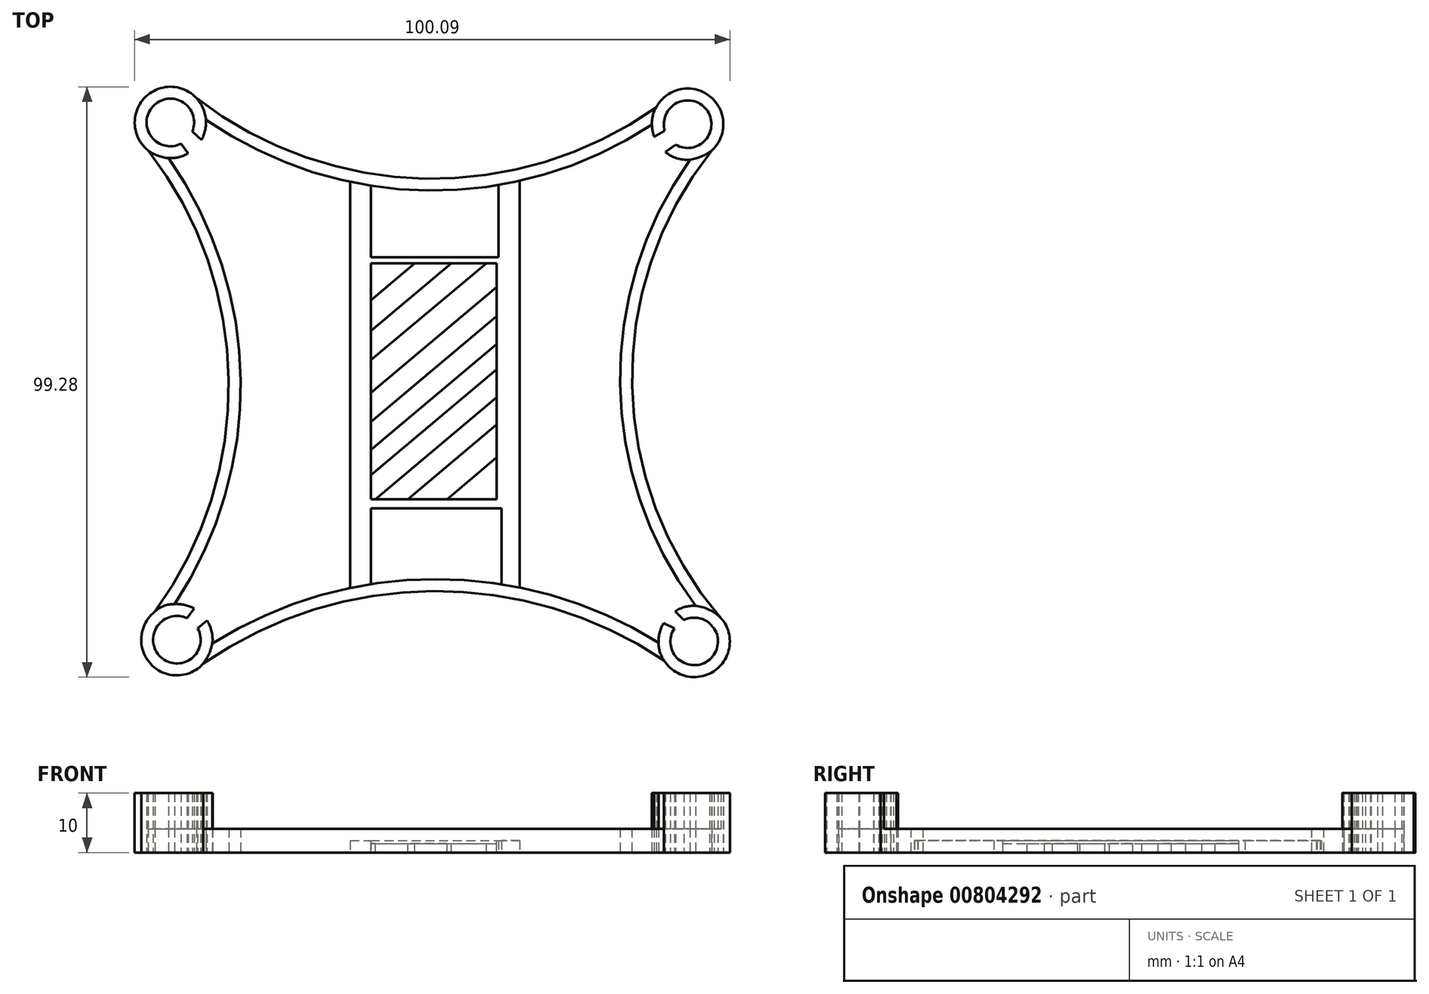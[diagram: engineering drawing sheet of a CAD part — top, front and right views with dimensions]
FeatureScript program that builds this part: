
annotation { "Feature Type Name" : "Feature", "Feature Type Description" : "" }
export const myFeature = defineFeature(function(context is Context, id is Id, definition is map)
    precondition{}
    {
        {
            var Q0;
            Q0=qCreatedBy(makeId("Top.planeOp"),FACE);
            var sketch = newSketch(context, id + "F0", { "sketchPlane" : qUnion([Q0])});
            skArc(sketch, "E0", {"start": v(-60.97, -47.72) * mm, "mid": v(-62.57, -47.1) * mm, "end": v(-64.27, -46.97) * mm});
            skArc(sketch, "E1", {"start": v(-59.74, 31.13) * mm, "mid": v(-59.13, 32.76) * mm, "end": v(-59.01, 34.49) * mm});
            skArc(sketch, "E2", {"start": v(18.25, 29.07) * mm, "mid": v(20.2, 28.03) * mm, "end": v(22.39, 27.76) * mm});
            skArc(sketch, "E3", {"start": v(17.97, -50.15) * mm, "mid": v(17.3, -51.75) * mm, "end": v(17.1, -53.47) * mm});
            skArc(sketch, "E4", {"start": v(-67.59, -48.23) * mm, "mid": v(-55.17, -9.25) * mm, "end": v(-68.73, 29.34) * mm});
            skArc(sketch, "E5", {"start": v(18.02, -56.44) * mm, "mid": v(-20.8, -44.78) * mm, "end": v(-59.45, -56.99) * mm});
            skArc(sketch, "E6", {"start": v(26.1, 29.36) * mm, "mid": v(12.66, -10.62) * mm, "end": v(28.07, -49.88) * mm});
            skArc(sketch, "E7", {"start": v(-60.63, 38.15) * mm, "mid": v(-22.22, 24.6) * mm, "end": v(16.7, 36.57) * mm});
            skLineSegment(sketch, "E8", {"start": v(-22.22, 24.6) * mm, "end": v(-20.8, -44.78) * mm, "construction": true});
            skLineSegment(sketch, "E9", {"start": v(-55.17, -9.82) * mm, "end": v(12.64, -9.82) * mm, "construction": true});
            skPoint(sketch, "E9.startSnap0", {"position": v(12.64, -9.82) * mm});
            skArc(sketch, "E10.0", {"start": v(-61.3, 32.5) * mm, "mid": v(-67.93, 36.75) * mm, "end": v(-63.18, 30.47) * mm});
            skArc(sketch, "E11.0", {"start": v(19.97, 30.3) * mm, "mid": v(25.16, 36.2) * mm, "end": v(18.17, 32.62) * mm});
            skArc(sketch, "E12.0", {"start": v(19.77, -51.03) * mm, "mid": v(23.06, -57.25) * mm, "end": v(26.48, -51.1) * mm});
            skArc(sketch, "E13.0", {"start": v(-62.16, -49.36) * mm, "mid": v(-66.65, -55.86) * mm, "end": v(-60.39, -51.03) * mm});
            skArc(sketch, "E14.0", {"start": v(-59.01, 34.49) * mm, "mid": v(-21.63, 22.59) * mm, "end": v(16, 33.66) * mm});
            skArc(sketch, "E15.0", {"start": v(-64.27, -46.97) * mm, "mid": v(-53.17, -9.3) * mm, "end": v(-65.28, 28.04) * mm});
            skArc(sketch, "E16.0", {"start": v(17.1, -53.47) * mm, "mid": v(-20.43, -42.78) * mm, "end": v(-57.93, -53.6) * mm});
            skArc(sketch, "E17.0", {"start": v(25.58, 31.89) * mm, "mid": v(25.53, 31.83) * mm, "end": v(25.48, 31.77) * mm});
            skLineSegment(sketch, "E18", {"start": v(18.17, 32.62) * mm, "end": v(16.39, 31.64) * mm});
            skLineSegment(sketch, "E19", {"start": v(19.97, 30.3) * mm, "end": v(18.25, 29.07) * mm});
            skArc(sketch, "E20.trimOffspring", {"start": v(22.39, 27.76) * mm, "mid": v(10.64, -9.9) * mm, "end": v(23.35, -47.25) * mm});
            skArc(sketch, "E21.trimOffspring", {"start": v(26.1, 29.36) * mm, "mid": v(25.66, 38.5) * mm, "end": v(16.7, 36.57) * mm});
            skArc(sketch, "E22.trimOffspring", {"start": v(16, 33.66) * mm, "mid": v(16.1, 32.63) * mm, "end": v(16.39, 31.64) * mm});
            skLineSegment(sketch, "E23", {"start": v(-63.18, 30.47) * mm, "end": v(-62, 28.84) * mm});
            skLineSegment(sketch, "E24", {"start": v(-61.3, 32.5) * mm, "end": v(-59.74, 31.13) * mm});
            skArc(sketch, "E25.trimOffspring", {"start": v(-65.28, 28.04) * mm, "mid": v(-63.58, 28.2) * mm, "end": v(-62, 28.84) * mm});
            skArc(sketch, "E26.trimOffspring", {"start": v(-60.63, 38.15) * mm, "mid": v(-69.4, 38.1) * mm, "end": v(-68.73, 29.34) * mm});
            skLineSegment(sketch, "E27", {"start": v(-62.16, -49.36) * mm, "end": v(-60.97, -47.72) * mm});
            skLineSegment(sketch, "E28", {"start": v(-60.39, -51.03) * mm, "end": v(-58.83, -49.74) * mm});
            skArc(sketch, "E29.trimOffspring", {"start": v(-57.93, -53.6) * mm, "mid": v(-58.05, -51.6) * mm, "end": v(-58.83, -49.74) * mm});
            skArc(sketch, "E30.trimOffspring", {"start": v(-67.59, -48.23) * mm, "mid": v(-68.3, -57.04) * mm, "end": v(-59.45, -56.99) * mm});
            skLineSegment(sketch, "E31", {"start": v(19.77, -51.03) * mm, "end": v(17.97, -50.15) * mm});
            skLineSegment(sketch, "E32", {"start": v(21.37, -49.64) * mm, "end": v(19.89, -48.18) * mm});
            skArc(sketch, "E33.trimOffspring", {"start": v(18.02, -56.44) * mm, "mid": v(26.39, -58.27) * mm, "end": v(28.07, -49.88) * mm});
            skArc(sketch, "E34.trimOffspring", {"start": v(25.72, -50.22) * mm, "mid": v(26.1, -50.66) * mm, "end": v(26.48, -51.1) * mm});
            skArc(sketch, "E35.trimOffspring", {"start": v(25.72, -50.22) * mm, "mid": v(23.63, -49.28) * mm, "end": v(21.37, -49.64) * mm});
            skArc(sketch, "E36.trimOffspring", {"start": v(23.35, -47.25) * mm, "mid": v(21.55, -47.45) * mm, "end": v(19.89, -48.18) * mm});
            skArc(sketch, "E37", {"start": v(-59.01, 34.49) * mm, "mid": v(-59.52, 36.45) * mm, "end": v(-60.63, 38.15) * mm});
            skArc(sketch, "E38", {"start": v(16.7, 36.57) * mm, "mid": v(16.14, 35.17) * mm, "end": v(16, 33.66) * mm});
            skArc(sketch, "E39", {"start": v(22.39, 27.76) * mm, "mid": v(24.34, 28.32) * mm, "end": v(26.1, 29.36) * mm});
            skArc(sketch, "E40", {"start": v(28.07, -49.88) * mm, "mid": v(25.97, -48.1) * mm, "end": v(23.35, -47.25) * mm});
            skArc(sketch, "E41", {"start": v(17.1, -53.47) * mm, "mid": v(17.33, -55.02) * mm, "end": v(18.02, -56.44) * mm});
            skArc(sketch, "E42", {"start": v(-64.27, -46.97) * mm, "mid": v(-66.06, -47.26) * mm, "end": v(-67.59, -48.23) * mm});
            skArc(sketch, "E43", {"start": v(-59.45, -56.99) * mm, "mid": v(-58.5, -55.37) * mm, "end": v(-57.93, -53.6) * mm});
            skArc(sketch, "E44", {"start": v(-68.73, 29.34) * mm, "mid": v(-67.1, 28.44) * mm, "end": v(-65.28, 28.04) * mm});
            skSolve(sketch);
        }
        {
            var Q0;
            Q0=makeQuery(id+"F0.imprint","IMPRINT",FACE,{"disambiguationData":[TD([[makeQuery(id+"F0.imprint","IMPRINT",EDGE,{"derivedFrom":sQuery(id+"F0.wireOp",EDGE,"E0")}),1.0]])]});
            var Q1;
            Q1=makeQuery(id+"F0.imprint","IMPRINT",FACE,{"disambiguationData":[TD([[makeQuery(id+"F0.imprint","IMPRINT",EDGE,{"derivedFrom":sQuery(id+"F0.wireOp",EDGE,"E3")}),1.0]])]});
            var Q2;
            Q2=makeQuery(id+"F0.imprint","IMPRINT",FACE,{"disambiguationData":[TD([[makeQuery(id+"F0.imprint","IMPRINT",EDGE,{"derivedFrom":sQuery(id+"F0.wireOp",EDGE,"E2")}),1.0]])]});
            var Q3;
            Q3=makeQuery(id+"F0.imprint","IMPRINT",FACE,{"disambiguationData":[TD([[makeQuery(id+"F0.imprint","IMPRINT",EDGE,{"derivedFrom":sQuery(id+"F0.wireOp",EDGE,"E1")}),1.0]])]});
            extrude(context, id + "F1", {"entities" : qUnion([Q0, Q1, Q2, Q3]), "depth" : 10 * mm, "offsetDistance" : 25.4 * mm});
        }
        {
            var Q0;
            Q0=makeQuery(id+"F0.imprint","IMPRINT",FACE,{"disambiguationData":[TD([[makeQuery(id+"F0.imprint","IMPRINT",EDGE,{"derivedFrom":sQuery(id+"F0.wireOp",EDGE,"E4")}),-1.0]])]});
            var Q1;
            Q1=makeQuery(id+"F0.imprint","IMPRINT",FACE,{"disambiguationData":[TD([[makeQuery(id+"F0.imprint","IMPRINT",EDGE,{"derivedFrom":sQuery(id+"F0.wireOp",EDGE,"E7")}),-1.0]])]});
            var Q2;
            {var subQ4=sQuery(id+"F0.wireOp",EDGE,"E20.trimOffspring");Q2=makeQuery(id+"F0.imprint","IMPRINT",FACE,{"disambiguationData":[TD([[makeQuery(id+"F0.imprint","IMPRINT",EDGE,{"derivedFrom":subQ4}),1.0]])]});}
            var Q3;
            Q3=makeQuery(id+"F0.imprint","IMPRINT",FACE,{"disambiguationData":[TD([[makeQuery(id+"F0.imprint","IMPRINT",EDGE,{"derivedFrom":sQuery(id+"F0.wireOp",EDGE,"E5")}),-1.0]])]});
            extrude(context, id + "F2", {"entities" : qUnion([Q0, Q1, Q2, Q3]), "operationType" : NewBodyOperationType.ADD, "depth" : 4 * mm, "offsetDistance" : 25.4 * mm});
        }
        {
            var Q0;
            {var subQ0=sQuery(id+"F0.wireOp",EDGE,"E38");var subQ1=sQuery(id+"F0.wireOp",EDGE,"E37");var subQ2=sQuery(id+"F0.wireOp",EDGE,"E40");var subQ3=sQuery(id+"F0.wireOp",EDGE,"E39");var subQ4=sQuery(id+"F0.wireOp",EDGE,"E6");var subQ5=sQuery(id+"F0.wireOp",EDGE,"E43");var subQ6=sQuery(id+"F0.wireOp",EDGE,"E41");var subQ7=sQuery(id+"F0.wireOp",EDGE,"E42");var subQ8=sQuery(id+"F0.wireOp",EDGE,"bHAAcOBc-Vqa3-5FWF-VtHR-RmdmbVXKJXTf");Q0=makeQuery(id+"F2.boolean.opBoolean","MERGE",FACE,{"derivedFrom":[makeQuery(id+"F1.opExtrude","CAP_FACE",FACE,{"disambiguationData":[OSD([sQuery(id+"F0.wireOp",EDGE,"E0"),sQuery(id+"F0.wireOp",EDGE,"E13.0"),sQuery(id+"F0.wireOp",EDGE,"E27"),sQuery(id+"F0.wireOp",EDGE,"E28"),sQuery(id+"F0.wireOp",EDGE,"E29.trimOffspring"),sQuery(id+"F0.wireOp",EDGE,"E30.trimOffspring"),subQ7,subQ5])],"isStart":true}),makeQuery(id+"F1.opExtrude","CAP_FACE",FACE,{"disambiguationData":[OSD([sQuery(id+"F0.wireOp",EDGE,"E1"),sQuery(id+"F0.wireOp",EDGE,"E10.0"),sQuery(id+"F0.wireOp",EDGE,"E23"),sQuery(id+"F0.wireOp",EDGE,"E24"),sQuery(id+"F0.wireOp",EDGE,"E25.trimOffspring"),sQuery(id+"F0.wireOp",EDGE,"E26.trimOffspring"),subQ1,subQ8])],"isStart":true}),makeQuery(id+"F1.opExtrude","CAP_FACE",FACE,{"disambiguationData":[OSD([sQuery(id+"F0.wireOp",EDGE,"E2"),sQuery(id+"F0.wireOp",EDGE,"E11.0"),sQuery(id+"F0.wireOp",EDGE,"E18"),sQuery(id+"F0.wireOp",EDGE,"E19"),sQuery(id+"F0.wireOp",EDGE,"E21.trimOffspring"),sQuery(id+"F0.wireOp",EDGE,"E22.trimOffspring"),subQ0,subQ3])],"isStart":true}),makeQuery(id+"F1.opExtrude","CAP_FACE",FACE,{"disambiguationData":[OSD([sQuery(id+"F0.wireOp",EDGE,"E3"),subQ4,sQuery(id+"F0.wireOp",EDGE,"E12.0"),sQuery(id+"F0.wireOp",EDGE,"E31"),sQuery(id+"F0.wireOp",EDGE,"E32"),sQuery(id+"F0.wireOp",EDGE,"E33.trimOffspring"),sQuery(id+"F0.wireOp",EDGE,"E34.trimOffspring"),sQuery(id+"F0.wireOp",EDGE,"E35.trimOffspring"),sQuery(id+"F0.wireOp",EDGE,"E36.trimOffspring"),subQ2,subQ6])],"isStart":true}),makeQuery(id+"F2.opExtrude","CAP_FACE",FACE,{"disambiguationData":[OSD([sQuery(id+"F0.wireOp",EDGE,"E4"),sQuery(id+"F0.wireOp",EDGE,"E15.0"),subQ8,subQ7])],"isStart":true}),makeQuery(id+"F2.opExtrude","CAP_FACE",FACE,{"disambiguationData":[OSD([sQuery(id+"F0.wireOp",EDGE,"E5"),sQuery(id+"F0.wireOp",EDGE,"E16.0"),subQ6,subQ5])],"isStart":true}),makeQuery(id+"F2.opExtrude","CAP_FACE",FACE,{"disambiguationData":[OSD([subQ4,sQuery(id+"F0.wireOp",EDGE,"E20.trimOffspring"),subQ3,subQ2])],"isStart":true}),makeQuery(id+"F2.opExtrude","CAP_FACE",FACE,{"disambiguationData":[OSD([sQuery(id+"F0.wireOp",EDGE,"E7"),sQuery(id+"F0.wireOp",EDGE,"E14.0"),subQ1,subQ0])],"isStart":true})]});}
            var sketch = newSketch(context, id + "F3", { "sketchPlane" : qUnion([Q0])});
            skLineSegment(sketch, "E45", {"start": v(-20.2, 42.78) * mm, "end": v(-20.43, -22.59) * mm, "construction": true});
            skPoint(sketch, "E45.startSnap0", {"position": v(-20.43, 42.78) * mm});
            skPoint(sketch, "E45.endSnap0", {"position": v(-20.43, 42.78) * mm});
            skLineSegment(sketch, "E46", {"start": v(-53.17, 9.3) * mm, "end": v(10.64, 9.3) * mm, "construction": true});
            skLineSegment(sketch, "E47.bottom", {"start": v(-31.28, 30.85) * mm, "end": v(-9.32, 30.85) * mm});
            skLineSegment(sketch, "E47.top", {"start": v(-31.28, -11.38) * mm, "end": v(-9.82, -11.38) * mm});
            skLineSegment(sketch, "E47.left", {"start": v(-34.74, 30.85) * mm, "end": v(-34.74, -11.38) * mm});
            skLineSegment(sketch, "E47.right", {"start": v(-6.24, 30.85) * mm, "end": v(-6.24, -11.38) * mm});
            skLineSegment(sketch, "E48", {"start": v(-6.24, 30.85) * mm, "end": v(-6.24, 44.2) * mm});
            skLineSegment(sketch, "E49", {"start": v(-6.24, -11.38) * mm, "end": v(-6.24, -24.2) * mm});
            skLineSegment(sketch, "E50", {"start": v(-34.74, 30.85) * mm, "end": v(-34.74, 44.27) * mm});
            skLineSegment(sketch, "E51", {"start": v(-34.74, -11.38) * mm, "end": v(-34.74, -24.03) * mm});
            skLineSegment(sketch, "E52", {"start": v(-31.28, 30.85) * mm, "end": v(-31.28, 43.63) * mm});
            skLineSegment(sketch, "E53", {"start": v(-31.28, -11.38) * mm, "end": v(-31.28, -23.4) * mm});
            skLineSegment(sketch, "E54", {"start": v(-9.32, 30.85) * mm, "end": v(-9.32, 43.64) * mm});
            skLineSegment(sketch, "E55", {"start": v(-9.82, -11.38) * mm, "end": v(-9.82, -23.5) * mm});
            skSolve(sketch);
        }
        {
            var Q0;
            Q0=makeQuery(id+"F3.imprint","IMPRINT",FACE,{"disambiguationData":[TD([[makeQuery(id+"F3.imprint","IMPRINT",EDGE,{"derivedFrom":sQuery(id+"F3.wireOp",EDGE,"E47.bottom")}),-1.0]])]});
            extrude(context, id + "F4", {"entities" : qUnion([Q0]), "operationType" : NewBodyOperationType.ADD, "oppositeDirection" : true, "depth" : 2 * mm, "offsetDistance" : 25.4 * mm});
        }
        {
            var Q0;
            Q0=makeQuery(id+"F4.opExtrude","CAP_FACE",FACE,{"disambiguationData":[OSD([sQuery(id+"F0.wireOp",EDGE,"E14.0"),sQuery(id+"F0.wireOp",EDGE,"E16.0"),sQuery(id+"F3.wireOp",EDGE,"E47.bottom"),sQuery(id+"F3.wireOp",EDGE,"E47.top"),sQuery(id+"F3.wireOp",EDGE,"E47.left"),sQuery(id+"F3.wireOp",EDGE,"E47.right"),sQuery(id+"F3.wireOp",EDGE,"E48"),sQuery(id+"F3.wireOp",EDGE,"E49"),sQuery(id+"F3.wireOp",EDGE,"E50"),sQuery(id+"F3.wireOp",EDGE,"E51"),sQuery(id+"F3.wireOp",EDGE,"E52"),sQuery(id+"F3.wireOp",EDGE,"E53"),sQuery(id+"F3.wireOp",EDGE,"E54"),sQuery(id+"F3.wireOp",EDGE,"E55")])],"isStart":false});
            var sketch = newSketch(context, id + "F5", { "sketchPlane" : qUnion([Q0])});
            skLineSegment(sketch, "E56", {"start": v(-31.28, -29.31) * mm, "end": v(-31.28, 10.36) * mm});
            skLineSegment(sketch, "E57", {"start": v(-31.28, 10.36) * mm, "end": v(-10.1, 10.36) * mm});
            skLineSegment(sketch, "E58", {"start": v(-10.1, 10.36) * mm, "end": v(-10.1, -29.31) * mm});
            skLineSegment(sketch, "E59", {"start": v(-10.1, -29.31) * mm, "end": v(-31.28, -29.31) * mm});
            skSolve(sketch);
        }
        {
            var Q0;
            Q0=makeQuery(id+"F5.imprint","IMPRINT",FACE,{"disambiguationData":[TD([[makeQuery(id+"F5.imprint","IMPRINT",EDGE,{"derivedFrom":sQuery(id+"F5.wireOp",EDGE,"E56")}),-1.0]])]});
            extrude(context, id + "F6", {"entities" : qUnion([Q0]), "operationType" : NewBodyOperationType.REMOVE, "oppositeDirection" : true, "depth" : .5 * mm, "offsetDistance" : 25.4 * mm});
        }
        {
            var Q0;
            Q0=makeQuery(id+"F6.boolean.opBoolean","COPY",FACE,{"derivedFrom":makeQuery(id+"F6.opExtrude","CAP_FACE",FACE,{"disambiguationData":[OSD([sQuery(id+"F5.wireOp",EDGE,"E56"),sQuery(id+"F5.wireOp",EDGE,"E57"),sQuery(id+"F5.wireOp",EDGE,"E58"),sQuery(id+"F5.wireOp",EDGE,"E59")])],"isStart":false})});
            var sketch = newSketch(context, id + "F7", { "sketchPlane" : qUnion([Q0])});
            skLineSegment(sketch, "E60", {"start": v(-31.28, 4.15) * mm, "end": v(-23.89, 10.36) * mm});
            skLineSegment(sketch, "E61", {"start": v(-31.28, -1.01) * mm, "end": v(-17.73, 10.36) * mm});
            skLineSegment(sketch, "E62", {"start": v(-31.28, -5.94) * mm, "end": v(-11.86, 10.36) * mm});
            skLineSegment(sketch, "E63", {"start": v(-31.28, -11.4) * mm, "end": v(-10.1, 6.37) * mm});
            skLineSegment(sketch, "E64", {"start": v(-31.28, -16.33) * mm, "end": v(-10.1, 1.45) * mm});
            skLineSegment(sketch, "E65", {"start": v(-31.28, -21.02) * mm, "end": v(-10.1, -3.24) * mm});
            skLineSegment(sketch, "E66", {"start": v(-31.28, -25.24) * mm, "end": v(-10.1, -7.47) * mm});
            skLineSegment(sketch, "E67", {"start": v(-30.52, -29.31) * mm, "end": v(-10.1, -12.17) * mm});
            skLineSegment(sketch, "E68", {"start": v(-25.05, -29.31) * mm, "end": v(-10.1, -16.77) * mm});
            skLineSegment(sketch, "E69", {"start": v(-18.43, -29.31) * mm, "end": v(-10.1, -22.32) * mm});
            skSolve(sketch);
        }
        {
            var Q0;
            {var subQ0=sQuery(id+"F7.wireOp",EDGE,"E60");Q0=makeQuery(id+"F7.imprint","IMPRINT",FACE,{"disambiguationData":[TD([[makeQuery(id+"F7.imprint","IMPRINT",EDGE,{"derivedFrom":subQ0}),1.0]])]});}
            var Q1;
            {var subQ0=sQuery(id+"F7.wireOp",EDGE,"E61");Q1=makeQuery(id+"F7.imprint","IMPRINT",FACE,{"disambiguationData":[TD([[makeQuery(id+"F7.imprint","IMPRINT",EDGE,{"derivedFrom":subQ0}),-1.0]])]});}
            var Q2;
            {var subQ0=sQuery(id+"F7.wireOp",EDGE,"E63");Q2=makeQuery(id+"F7.imprint","IMPRINT",FACE,{"disambiguationData":[TD([[makeQuery(id+"F7.imprint","IMPRINT",EDGE,{"derivedFrom":subQ0}),-1.0]])]});}
            var Q3;
            {var subQ0=sQuery(id+"F7.wireOp",EDGE,"E65");Q3=makeQuery(id+"F7.imprint","IMPRINT",FACE,{"disambiguationData":[TD([[makeQuery(id+"F7.imprint","IMPRINT",EDGE,{"derivedFrom":subQ0}),-1.0]])]});}
            var Q4;
            {var subQ0=sQuery(id+"F7.wireOp",EDGE,"E67");Q4=makeQuery(id+"F7.imprint","IMPRINT",FACE,{"disambiguationData":[TD([[makeQuery(id+"F7.imprint","IMPRINT",EDGE,{"derivedFrom":subQ0}),-1.0]])]});}
            var Q5;
            {var subQ0=sQuery(id+"F7.wireOp",EDGE,"E69");Q5=makeQuery(id+"F7.imprint","IMPRINT",FACE,{"disambiguationData":[TD([[makeQuery(id+"F7.imprint","IMPRINT",EDGE,{"derivedFrom":subQ0}),-1.0]])]});}
            extrude(context, id + "F8", {"entities" : qUnion([Q0, Q1, Q2, Q3, Q4, Q5]), "operationType" : NewBodyOperationType.REMOVE, "endBound" : BoundingType.THROUGH_ALL, "oppositeDirection" : true, "depth" : 25.4 * mm, "offsetDistance" : 25.4 * mm});
        }
    });
